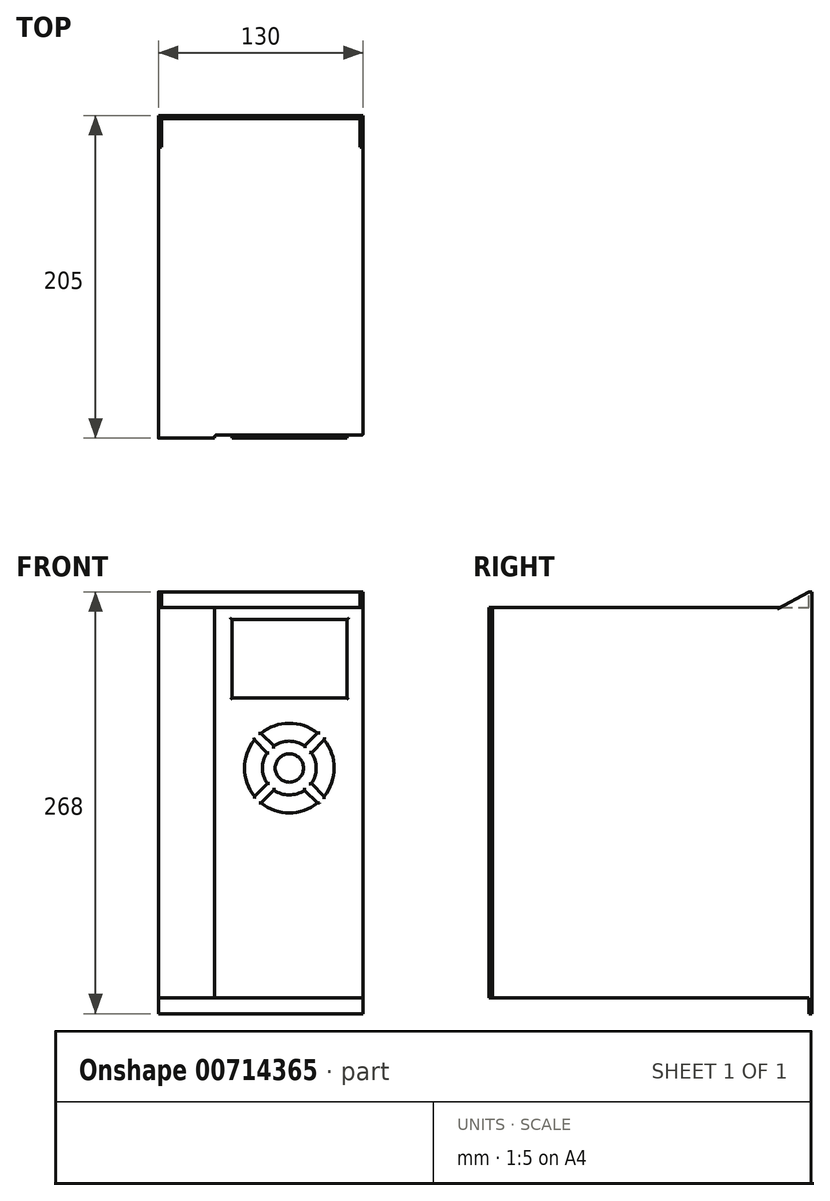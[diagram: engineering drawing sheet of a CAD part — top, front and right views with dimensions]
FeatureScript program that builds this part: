
annotation { "Feature Type Name" : "Feature", "Feature Type Description" : "" }
export const myFeature = defineFeature(function(context is Context, id is Id, definition is map)
    precondition{}
    {
        {
            var Q0;
            Q0=qCreatedBy(makeId("Front.planeOp"),FACE);
            var sketch = newSketch(context, id + "F0", { "sketchPlane" : qUnion([Q0])});
            skLineSegment(sketch, "E0.bottom", {"start": v(65, 124) * mm, "end": v(-65, 124) * mm});
            skLineSegment(sketch, "E0.top", {"start": v(65, -124) * mm, "end": v(-65, -124) * mm});
            skLineSegment(sketch, "E0.left", {"start": v(65, 124) * mm, "end": v(65, -124) * mm});
            skLineSegment(sketch, "E0.right", {"start": v(-65, 124) * mm, "end": v(-65, -124) * mm});
            skPoint(sketch, "E0.middle", {"position": v(0, 0) * mm});
            skSolve(sketch);
        }
        {
            var Q0;
            Q0=makeQuery(id+"F0.imprint","IMPRINT",FACE,{"disambiguationData":[TD([[makeQuery(id+"F0.imprint","IMPRINT",EDGE,{"derivedFrom":sQuery(id+"F0.wireOp",EDGE,"E0.bottom")}),1.0]])]});
            extrude(context, id + "F1", {"entities" : qUnion([Q0]), "depth" : 205 * mm, "offsetDistance" : 25 * mm});
        }
        {
            var Q0;
            Q0=makeQuery(id+"F1.opExtrude","CAP_FACE",FACE,{"disambiguationData":[OSD([sQuery(id+"F0.wireOp",EDGE,"E0.bottom"),sQuery(id+"F0.wireOp",EDGE,"E0.top"),sQuery(id+"F0.wireOp",EDGE,"E0.left"),sQuery(id+"F0.wireOp",EDGE,"E0.right")])],"isStart":false});
            var sketch = newSketch(context, id + "F2", { "sketchPlane" : qUnion([Q0])});
            skLineSegment(sketch, "E1.bottom", {"start": v(-18.3, 116.3) * mm, "end": v(54.8, 116.3) * mm});
            skLineSegment(sketch, "E1.top", {"start": v(-18.3, 66.5) * mm, "end": v(54.8, 66.5) * mm});
            skLineSegment(sketch, "E1.left", {"start": v(-18.3, 116.3) * mm, "end": v(-18.3, 66.5) * mm});
            skLineSegment(sketch, "E1.right", {"start": v(54.8, 116.3) * mm, "end": v(54.8, 66.5) * mm});
            skArc(sketch, "E2", {"start": v(-4.12, 39.81) * mm, "mid": v(-10.38, 21.94) * mm, "end": v(-4.04, 4.09) * mm});
            skLineSegment(sketch, "E3.0", {"start": v(40.29, 3.89) * mm, "end": v(32.05, 12.13) * mm});
            skLineSegment(sketch, "E4.0", {"start": v(36.05, -0.36) * mm, "end": v(27.77, 7.92) * mm});
            skLineSegment(sketch, "E5.0", {"start": v(0, -0.36) * mm, "end": v(8.35, 8) * mm});
            skLineSegment(sketch, "E6.0", {"start": v(-4.24, 3.89) * mm, "end": v(4.1, 12.24) * mm});
            skArc(sketch, "E7.trimOffspring", {"start": v(36.02, 44.15) * mm, "mid": v(18.05, 50.49) * mm, "end": v(0.1, 44.07) * mm});
            skArc(sketch, "E8.trimOffspring", {"start": v(0.2, -0.15) * mm, "mid": v(18.05, -6.49) * mm, "end": v(35.93, -0.23) * mm});
            skArc(sketch, "E9.trimOffspring", {"start": v(40.19, 4) * mm, "mid": v(46.6, 21.94) * mm, "end": v(40.27, 39.91) * mm});
            skLineSegment(sketch, "E10.trimOffspring", {"start": v(4.03, 31.66) * mm, "end": v(-4.24, 39.93) * mm});
            skLineSegment(sketch, "E11.trimOffspring", {"start": v(32.12, 31.76) * mm, "end": v(40.29, 39.93) * mm});
            skLineSegment(sketch, "E12.trimOffspring", {"start": v(27.88, 36) * mm, "end": v(36.05, 44.18) * mm});
            skLineSegment(sketch, "E13.trimOffspring", {"start": v(8.24, 35.93) * mm, "end": v(0, 44.18) * mm});
            skCircle(sketch, "E14", {"center": v(18.11, 22) * mm, "radius": 9 * mm});
            skArc(sketch, "E15", {"start": v(4.03, 31.66) * mm, "mid": v(1.04, 21.94) * mm, "end": v(4.1, 12.24) * mm});
            skArc(sketch, "E16.trimOffspring", {"start": v(8.35, 8) * mm, "mid": v(18.05, 4.93) * mm, "end": v(27.77, 7.92) * mm});
            skArc(sketch, "E17.trimOffspring", {"start": v(32.05, 12.13) * mm, "mid": v(35.19, 21.94) * mm, "end": v(32.12, 31.76) * mm});
            skArc(sketch, "E18.trimOffspring", {"start": v(27.88, 36) * mm, "mid": v(18.05, 39.07) * mm, "end": v(8.24, 35.93) * mm});
            skLineSegment(sketch, "E19", {"start": v(-29.34, 124) * mm, "end": v(-29.34, -124) * mm});
            skSolve(sketch);
        }
        {
            var Q0;
            Q0=makeQuery(id+"F2.imprint","IMPRINT",FACE,{"disambiguationData":[TD([[makeQuery(id+"F2.imprint","IMPRINT",EDGE,{"derivedFrom":sQuery(id+"F2.wireOp",EDGE,"E1.bottom")}),1.0]])]});
            extrude(context, id + "F3", {"entities" : qUnion([Q0]), "operationType" : NewBodyOperationType.REMOVE, "oppositeDirection" : true, "depth" : 2 * mm, "offsetDistance" : 25 * mm});
        }
        {
            var Q0;
            Q0=makeQuery(id+"F1.opExtrude","CAP_FACE",FACE,{"disambiguationData":[OSD([sQuery(id+"F0.wireOp",EDGE,"E0.bottom"),sQuery(id+"F0.wireOp",EDGE,"E0.top"),sQuery(id+"F0.wireOp",EDGE,"E0.left"),sQuery(id+"F0.wireOp",EDGE,"E0.right")])],"isStart":true});
            var sketch = newSketch(context, id + "F4", { "sketchPlane" : qUnion([Q0])});
            skLineSegment(sketch, "E20.bottom", {"start": v(65, 134) * mm, "end": v(-65, 134) * mm});
            skLineSegment(sketch, "E20.top", {"start": v(65, -134) * mm, "end": v(-65, -134) * mm});
            skLineSegment(sketch, "E20.left", {"start": v(65, 134) * mm, "end": v(65, -134) * mm});
            skLineSegment(sketch, "E20.right", {"start": v(-65, 134) * mm, "end": v(-65, -134) * mm});
            skPoint(sketch, "E20.middle", {"position": v(0, 0) * mm});
            skSolve(sketch);
        }
        {
            var Q0;
            {var subQ6=sQuery(id+"F4.wireOp",EDGE,"E20.bottom");Q0=makeQuery(id+"F4.imprint","IMPRINT",FACE,{"disambiguationData":[TD([[makeQuery(id+"F4.imprint","IMPRINT",EDGE,{"derivedFrom":subQ6}),1.0]])]});}
            var Q1;
            {var subQ6=sQuery(id+"F4.wireOp",EDGE,"E20.top");Q1=makeQuery(id+"F4.imprint","IMPRINT",FACE,{"disambiguationData":[TD([[makeQuery(id+"F4.imprint","IMPRINT",EDGE,{"derivedFrom":subQ6}),-1.0]])]});}
            extrude(context, id + "F5", {"entities" : qUnion([Q0, Q1]), "operationType" : NewBodyOperationType.ADD, "oppositeDirection" : true, "depth" : 20 * mm, "offsetDistance" : 25 * mm});
        }
        {
            var Q0;
            Q0=makeQuery(id+"F5.opExtrude","SWEPT_FACE",FACE,{"disambiguationData":[OSD([sQuery(id+"F4.wireOp",EDGE,"E20.bottom")])]});
            var sketch = newSketch(context, id + "F6", { "sketchPlane" : qUnion([Q0])});
            skLineSegment(sketch, "E21.bottom", {"start": v(-65, 0) * mm, "end": v(-63, 0) * mm});
            skLineSegment(sketch, "E21.top", {"start": v(-65, -2) * mm, "end": v(-63, -2) * mm});
            skLineSegment(sketch, "E21.left", {"start": v(-65, 0) * mm, "end": v(-65, -2) * mm});
            skLineSegment(sketch, "E21.right", {"start": v(-63, 0) * mm, "end": v(-63, -2) * mm});
            skLineSegment(sketch, "E22.bottom", {"start": v(65, -20) * mm, "end": v(63, -20) * mm});
            skLineSegment(sketch, "E22.top", {"start": v(65, -18) * mm, "end": v(63, -18) * mm});
            skLineSegment(sketch, "E22.left", {"start": v(65, -20) * mm, "end": v(65, -18) * mm});
            skLineSegment(sketch, "E22.right", {"start": v(63, -20) * mm, "end": v(63, -18) * mm});
            skLineSegment(sketch, "E23.bottom", {"start": v(-63, -2) * mm, "end": v(63, -2) * mm});
            skLineSegment(sketch, "E23.top", {"start": v(-63, -20) * mm, "end": v(63, -20) * mm});
            skLineSegment(sketch, "E23.left", {"start": v(-63, -2) * mm, "end": v(-63, -20) * mm});
            skLineSegment(sketch, "E23.right", {"start": v(63, -2) * mm, "end": v(63, -20) * mm});
            skSolve(sketch);
        }
        {
            var Q0;
            {var subQ2=sQuery(id+"F6.wireOp",EDGE,"E23.bottom");Q0=makeQuery(id+"F6.imprint","IMPRINT",FACE,{"disambiguationData":[TD([[makeQuery(id+"F6.imprint","IMPRINT",EDGE,{"derivedFrom":subQ2}),-1.0]])]});}
            var Q1;
            Q1=makeQuery(id+"F1.opExtrude","SWEPT_FACE",FACE,{"disambiguationData":[OSD([sQuery(id+"F0.wireOp",EDGE,"E0.bottom")])]});
            extrude(context, id + "F7", {"entities" : qUnion([Q0]), "operationType" : NewBodyOperationType.REMOVE, "endBound" : BoundingType.UP_TO_SURFACE, "oppositeDirection" : true, "depth" : 25 * mm, "endBoundEntityFace" : qUnion([Q1]), "offsetDistance" : 25 * mm});
        }
        {
            var Q0;
            {var subQ0=sQuery(id+"F4.wireOp",EDGE,"E20.right");Q0=makeQuery(id+"F5.boolean.opBoolean","MERGE",FACE,{"derivedFrom":[makeQuery(id+"F1.opExtrude","SWEPT_FACE",FACE,{"disambiguationData":[OSD([sQuery(id+"F0.wireOp",EDGE,"E0.left")])]}),makeQuery(id+"F5.opExtrude","SWEPT_FACE",FACE,{"disambiguationData":[OSD([subQ0]),TDD([makeQuery(id+"F4.imprint","IMPRINT",EDGE,{"disambiguationData":[TD([[makeQuery(id+"F4.imprint","INTERSECT",VERTEX,{"derivedFrom":[makeQuery(id+"F1.opExtrude","CAP_EDGE",EDGE,{"disambiguationData":[OSD([sQuery(id+"F0.wireOp",EDGE,"E0.bottom")])],"isStart":true}),subQ0]}),1.0]])],"derivedFrom":subQ0})])]}),makeQuery(id+"F5.opExtrude","SWEPT_FACE",FACE,{"disambiguationData":[OSD([subQ0]),TDD([makeQuery(id+"F4.imprint","IMPRINT",EDGE,{"disambiguationData":[TD([[makeQuery(id+"F4.imprint","INTERSECT",VERTEX,{"derivedFrom":[makeQuery(id+"F1.opExtrude","CAP_EDGE",EDGE,{"disambiguationData":[OSD([sQuery(id+"F0.wireOp",EDGE,"E0.top")])],"isStart":true}),subQ0]}),-1.0]])],"derivedFrom":subQ0})])]})]});}
            var sketch = newSketch(context, id + "F8", { "sketchPlane" : qUnion([Q0])});
            skLineSegment(sketch, "E24", {"start": v(-20, 124) * mm, "end": v(-2, 134) * mm});
            skLineSegment(sketch, "E25", {"start": v(-2, 134) * mm, "end": v(0, 134) * mm});
            skSolve(sketch);
        }
        {
            var Q0;
            {var subQ0=sQuery(id+"F8.wireOp",EDGE,"E24");Q0=makeQuery(id+"F8.imprint","IMPRINT",FACE,{"disambiguationData":[TD([[makeQuery(id+"F8.imprint","IMPRINT",EDGE,{"derivedFrom":subQ0}),1.0]])]});}
            extrude(context, id + "F9", {"entities" : qUnion([Q0]), "operationType" : NewBodyOperationType.REMOVE, "endBound" : BoundingType.THROUGH_ALL, "oppositeDirection" : true, "depth" : 25 * mm, "offsetDistance" : 25 * mm});
        }
        {
            var Q0;
            Q0=makeQuery(id+"F1.opExtrude","SWEPT_EDGE",EDGE,{"disambiguationData":[OSD([sQuery(id+"F0.wireOp",EDGE,"E0.bottom"),sQuery(id+"F0.wireOp",EDGE,"E0.right")])]});
            var Q1;
            {var subQ0=sQuery(id+"F4.wireOp",EDGE,"E20.left");Q1=makeQuery(id+"F9.boolean.opBoolean","INTERSECT",EDGE,{"derivedFrom":[makeQuery(id+"F5.boolean.opBoolean","MERGE",FACE,{"derivedFrom":[makeQuery(id+"F1.opExtrude","SWEPT_FACE",FACE,{"disambiguationData":[OSD([sQuery(id+"F0.wireOp",EDGE,"E0.right")])]}),makeQuery(id+"F5.opExtrude","SWEPT_FACE",FACE,{"disambiguationData":[OSD([subQ0]),TDD([makeQuery(id+"F4.imprint","IMPRINT",EDGE,{"disambiguationData":[TD([[makeQuery(id+"F4.imprint","INTERSECT",VERTEX,{"derivedFrom":[makeQuery(id+"F1.opExtrude","CAP_EDGE",EDGE,{"disambiguationData":[OSD([sQuery(id+"F0.wireOp",EDGE,"E0.bottom")])],"isStart":true}),subQ0]}),1.0]])],"derivedFrom":subQ0})])]}),makeQuery(id+"F5.opExtrude","SWEPT_FACE",FACE,{"disambiguationData":[OSD([subQ0]),TDD([makeQuery(id+"F4.imprint","IMPRINT",EDGE,{"disambiguationData":[TD([[makeQuery(id+"F4.imprint","INTERSECT",VERTEX,{"derivedFrom":[makeQuery(id+"F1.opExtrude","CAP_EDGE",EDGE,{"disambiguationData":[OSD([sQuery(id+"F0.wireOp",EDGE,"E0.top")])],"isStart":true}),subQ0]}),-1.0]])],"derivedFrom":subQ0})])]})]}),makeQuery(id+"F9.opExtrude","SWEPT_FACE",FACE,{"disambiguationData":[OSD([sQuery(id+"F8.wireOp",EDGE,"E24")])]})]});}
            var Q2;
            Q2=makeQuery(id+"F9.boolean.opBoolean","COPY",EDGE,{"derivedFrom":makeQuery(id+"F9.opExtrude","CAP_EDGE",EDGE,{"disambiguationData":[OSD([sQuery(id+"F8.wireOp",EDGE,"E24")])],"isStart":true})});
            var Q3;
            Q3=makeQuery(id+"F1.opExtrude","SWEPT_EDGE",EDGE,{"disambiguationData":[OSD([sQuery(id+"F0.wireOp",EDGE,"E0.bottom"),sQuery(id+"F0.wireOp",EDGE,"E0.left")])]});
            var Q4;
            Q4=makeQuery(id+"F3.boolean.opBoolean","COPY",FACE,{"derivedFrom":makeQuery(id+"F3.opExtrude","CAP_FACE",FACE,{"disambiguationData":[OSD([sQuery(id+"F0.wireOp",EDGE,"E0.bottom"),sQuery(id+"F0.wireOp",EDGE,"E0.top"),sQuery(id+"F0.wireOp",EDGE,"E0.left"),sQuery(id+"F0.wireOp",EDGE,"E0.right"),sQuery(id+"F2.wireOp",EDGE,"E1.bottom"),sQuery(id+"F2.wireOp",EDGE,"E1.top"),sQuery(id+"F2.wireOp",EDGE,"E1.left"),sQuery(id+"F2.wireOp",EDGE,"E1.right"),sQuery(id+"F2.wireOp",EDGE,"E2"),sQuery(id+"F2.wireOp",EDGE,"E3.0"),sQuery(id+"F2.wireOp",EDGE,"E4.0"),sQuery(id+"F2.wireOp",EDGE,"E5.0"),sQuery(id+"F2.wireOp",EDGE,"E6.0"),sQuery(id+"F2.wireOp",EDGE,"E7.trimOffspring"),sQuery(id+"F2.wireOp",EDGE,"E8.trimOffspring"),sQuery(id+"F2.wireOp",EDGE,"E9.trimOffspring"),sQuery(id+"F2.wireOp",EDGE,"E10.trimOffspring"),sQuery(id+"F2.wireOp",EDGE,"E11.trimOffspring"),sQuery(id+"F2.wireOp",EDGE,"E12.trimOffspring"),sQuery(id+"F2.wireOp",EDGE,"E13.trimOffspring"),sQuery(id+"F2.wireOp",EDGE,"E14"),sQuery(id+"F2.wireOp",EDGE,"E15"),sQuery(id+"F2.wireOp",EDGE,"E16.trimOffspring"),sQuery(id+"F2.wireOp",EDGE,"E17.trimOffspring"),sQuery(id+"F2.wireOp",EDGE,"E18.trimOffspring")])],"isStart":false})});
            fillet(context, id + "F10", {"entities" : qUnion([Q0, Q1, Q2, Q3, Q4]), "radius" : 1 * mm, "tangentPropagation" : true, "allowEdgeOverflow" : false});
        }
        {
            var Q0;
            Q0=makeQuery(id+"F5.opExtrude","CAP_FACE",FACE,{"disambiguationData":[OSD([sQuery(id+"F0.wireOp",EDGE,"E0.top"),sQuery(id+"F4.wireOp",EDGE,"E20.top"),sQuery(id+"F4.wireOp",EDGE,"E20.left"),sQuery(id+"F4.wireOp",EDGE,"E20.right")])],"isStart":false});
            extrude(context, id + "F11", {"entities" : qUnion([Q0]), "operationType" : NewBodyOperationType.REMOVE, "oppositeDirection" : true, "depth" : 18 * mm, "offsetDistance" : 25 * mm});
        }
    });
